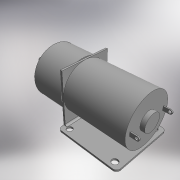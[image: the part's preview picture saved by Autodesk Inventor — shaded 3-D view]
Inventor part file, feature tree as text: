
AUTODESK INVENTOR PART (.ipt)
format: ipt  version: 2016 (Build 200138000, 138)  size: 253,440 bytes
history: native  units: mm
features: extrude x10, sketch x10, projected_geometry x7, fillet x3
ambient origin geometry x8: Origin, YZ Plane, XZ Plane, XY Plane, X Axis, Y Axis, Z Axis, Center Point
bodies: Solid1 (feature_tree)
feature tree (30):
  extrude  "Extrusion1"  Depth=30.0mm
  extrude  "Extrusion2"  Depth=3.0mm
  fillet  "Fillet1"  Radius=3.0mm
  extrude  "Extrusion3"  Depth=12.0mm
  extrude  "Extrusion4"  Depth=0.9mm TaperAngle=0.0deg
  extrude  "Extrusion5"  Depth=24.0mm
  extrude  "Extrusion6"  Depth=26.1mm TaperAngle=0.0deg
  extrude  "Extrusion7"  Depth=30.1mm
  fillet  "Fillet2"  Radius=24.0mm
  fillet  "Fillet3"  Radius=30.1mm
  extrude  "Extrusion8"  Depth=16.5mm TaperAngle=0.0deg
  extrude  "Extrusion9"  Depth=2.0mm TaperAngle=0.0deg
  extrude  "Extrusion10"  Depth=1.0mm
  sketch  "Sketch1"  dims[d0=31.0mm d1=30.0mm]
  sketch  "Sketch2"  dims[d2=15.0mm d3=15.5mm d4=3.0mm]
  projected_geometry  "Projected Loop1"
  sketch  "Sketch3"  dims[d5=12.0mm d6=12.0mm]
  projected_geometry  "Projected Loop2"
  sketch  "Sketch4"  dims[d7=2.0mm d8=0.9mm d9=0.0mm]
  projected_geometry  "Projected Loop3"
  sketch  "Sketch5"  dims[d10=0.9mm d11=24.0mm]
  projected_geometry  "Projected Loop4"
  sketch  "Sketch6"  dims[d12=12.0mm d13=26.1mm d14=0.0mm]
  projected_geometry  "Projected Loop5"
  sketch  "Sketch7"  dims[d15=1.0mm d16=15.0mm d17=24.0mm d18=30.1mm d19=0.0mm]
  projected_geometry  "Projected Loop6"
  sketch  "Sketch8"  dims[d20=25.0mm d21=16.5mm d22=0.0mm]
  sketch  "Sketch9"  dims[d23=8.5mm d24=2.0mm d25=0.0mm]
  sketch  "Sketch10"  dims[d26=2.0mm d27=1.0mm d28=0.5mm d29=9.25mm d30=4.0mm d31=0.0mm d32=1.5mm d33=1.05mm d34=4.0mm d35=0.0mm d36=1.0mm d37=1.0mm d38=4.97mm d39=6.0mm d40=0.0mm d41=1.98mm d42=6.5mm d43=0.0mm d44=3.0mm d45=0.5mm d46=1.0mm d47=6.5mm d48=0.0mm]
  projected_geometry  "Projected Loop7"
